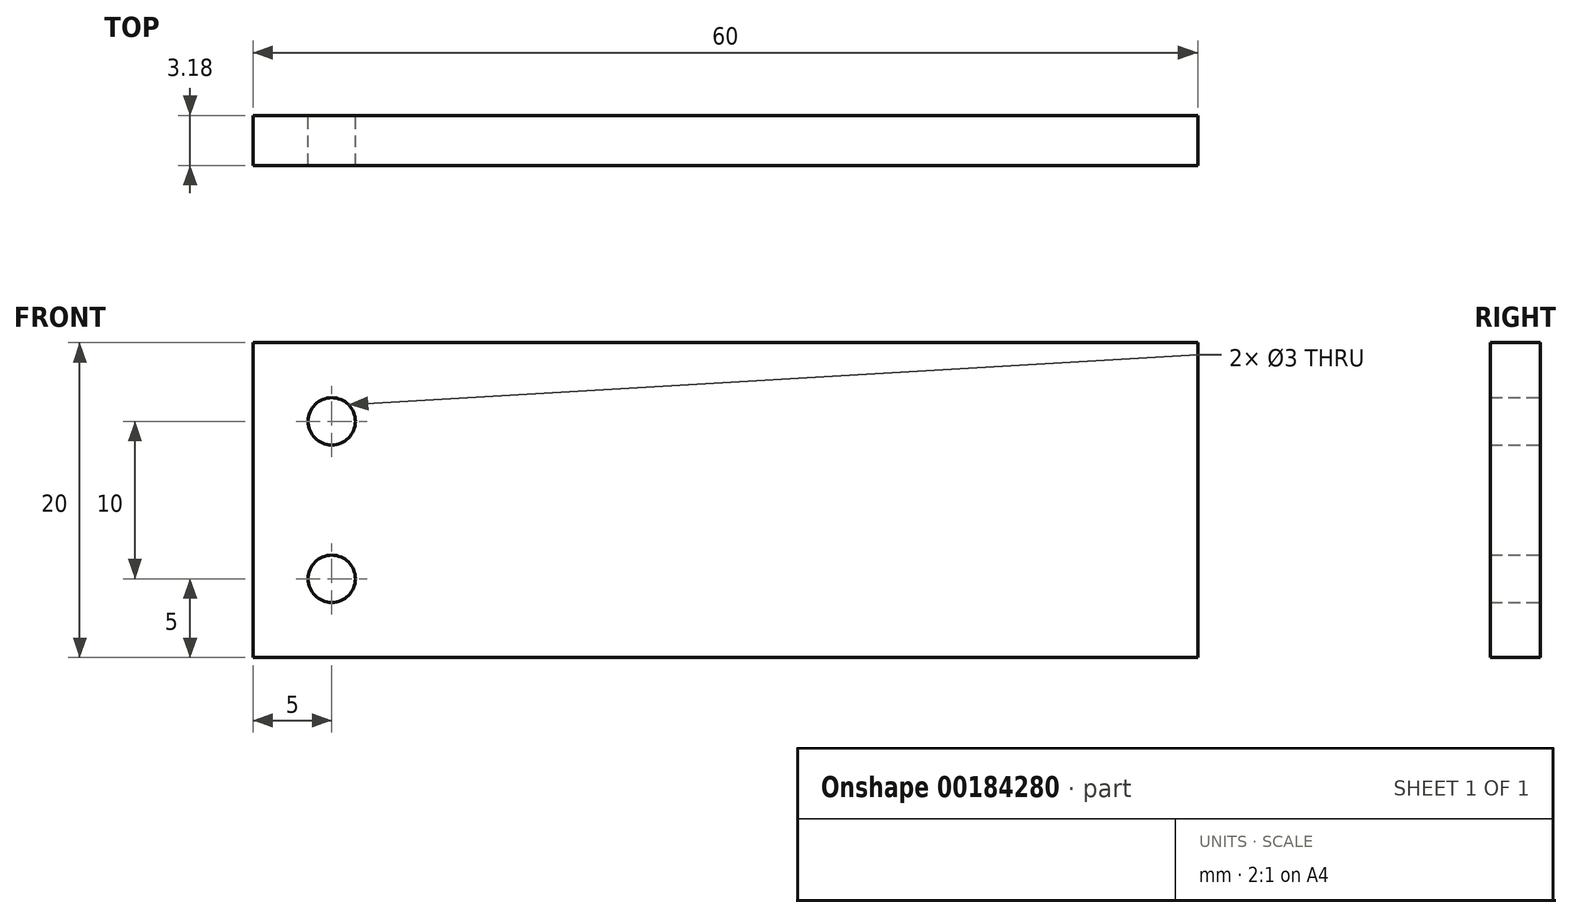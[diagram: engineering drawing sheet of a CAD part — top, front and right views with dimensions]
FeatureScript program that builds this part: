
annotation { "Feature Type Name" : "Feature", "Feature Type Description" : "" }
export const myFeature = defineFeature(function(context is Context, id is Id, definition is map)
    precondition{}
    {
        {
            var Q0;
            Q0=qCreatedBy(makeId("Front.planeOp"),FACE);
            var sketch = newSketch(context, id + "F0", { "sketchPlane" : qUnion([Q0])});
            skLineSegment(sketch, "E0.bottom", {"start": v(-30, 20) * mm, "end": v(30, 20) * mm});
            skLineSegment(sketch, "E0.top", {"start": v(-30, 0) * mm, "end": v(30, 0) * mm});
            skLineSegment(sketch, "E0.left", {"start": v(-30, 20) * mm, "end": v(-30, 0) * mm});
            skLineSegment(sketch, "E0.right", {"start": v(30, 20) * mm, "end": v(30, 0) * mm});
            skCircle(sketch, "E1", {"center": v(-25, 15) * mm, "radius": 1.5 * mm});
            skCircle(sketch, "E2", {"center": v(-25, 5) * mm, "radius": 1.5 * mm});
            skLineSegment(sketch, "E3", {"start": v(-30, 10) * mm, "end": v(30, 10) * mm, "construction": true});
            skSolve(sketch);
        }
        {
            var Q0;
            Q0=makeQuery(id+"F0.imprint","IMPRINT",FACE,{"disambiguationData":[TD([[makeQuery(id+"F0.imprint","IMPRINT",EDGE,{"derivedFrom":sQuery(id+"F0.wireOp",EDGE,"E0.bottom")}),-1.0]])]});
            extrude(context, id + "F1", {"entities" : qUnion([Q0]), "depth" : 3.17 * mm});
        }
    });
